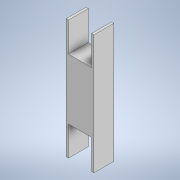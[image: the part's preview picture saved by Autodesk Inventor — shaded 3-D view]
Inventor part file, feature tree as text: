
AUTODESK INVENTOR PART (.ipt)
format: ipt  version: 2020 (Build 240168000, 168)  size: 129,536 bytes
history: native  units: mm
features: extrude x2, sketch x1
ambient origin geometry x8: Origin, YZ Plane, XZ Plane, XY Plane, X Axis, Y Axis, Z Axis, Center Point
bodies: Solid1 (feature_tree)
feature tree (3):
  extrude  "Extrusion1"  Depth=80.0mm
  extrude  "Extrusion2"  Depth=80.0mm
  sketch  "Sketch2"  dims[d0=70.0mm d1=80.0mm d2=80.0mm d3=6.0mm d4=50.0mm d5=0.0mm d7=6.0mm d8=140.0mm d9=0.0mm d10=70.0mm d6=0.5mm]
